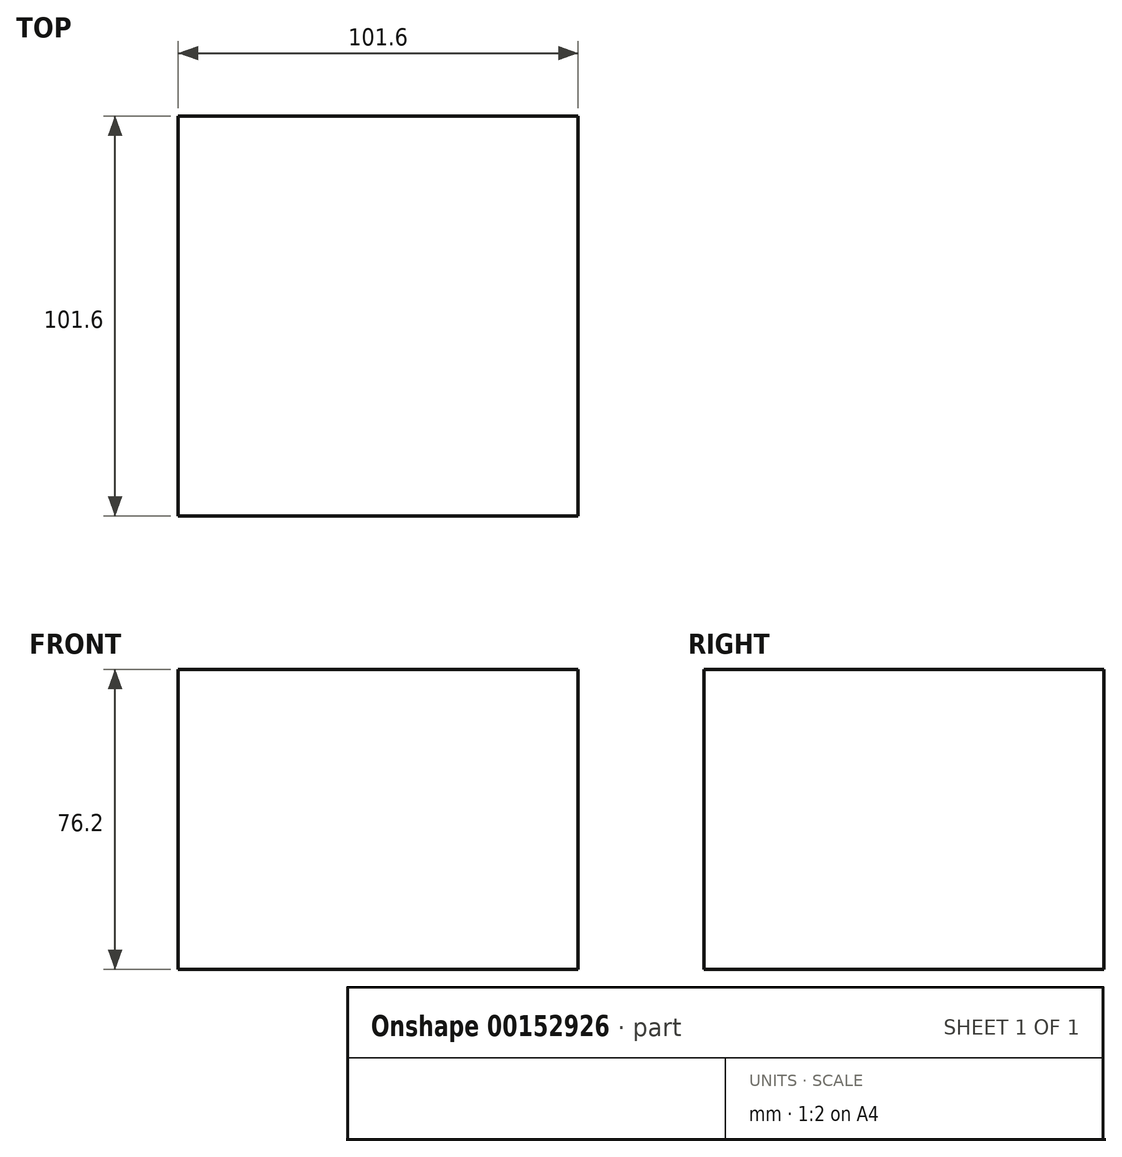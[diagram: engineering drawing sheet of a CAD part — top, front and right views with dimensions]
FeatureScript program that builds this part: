
annotation { "Feature Type Name" : "Feature", "Feature Type Description" : "" }
export const myFeature = defineFeature(function(context is Context, id is Id, definition is map)
    precondition{}
    {
        {
            var Q0;
            Q0=qCreatedBy(makeId("Top.planeOp"),FACE);
            var sketch = newSketch(context, id + "F0", { "sketchPlane" : qUnion([Q0])});
            skLineSegment(sketch, "E0.bottom", {"start": v(0, 0) * mm, "end": v(101.6, 0) * mm});
            skLineSegment(sketch, "E0.top", {"start": v(0, -101.6) * mm, "end": v(101.6, -101.6) * mm});
            skLineSegment(sketch, "E0.left", {"start": v(0, 0) * mm, "end": v(0, -101.6) * mm});
            skLineSegment(sketch, "E0.right", {"start": v(101.6, 0) * mm, "end": v(101.6, -101.6) * mm});
            skSolve(sketch);
        }
        {
            var Q0;
            Q0 = qSketchRegion(id + "F0", true);
            extrude(context, id + "F1", {"entities" : qUnion([Q0]), "depth" : 76.2 * mm});
        }
    });
